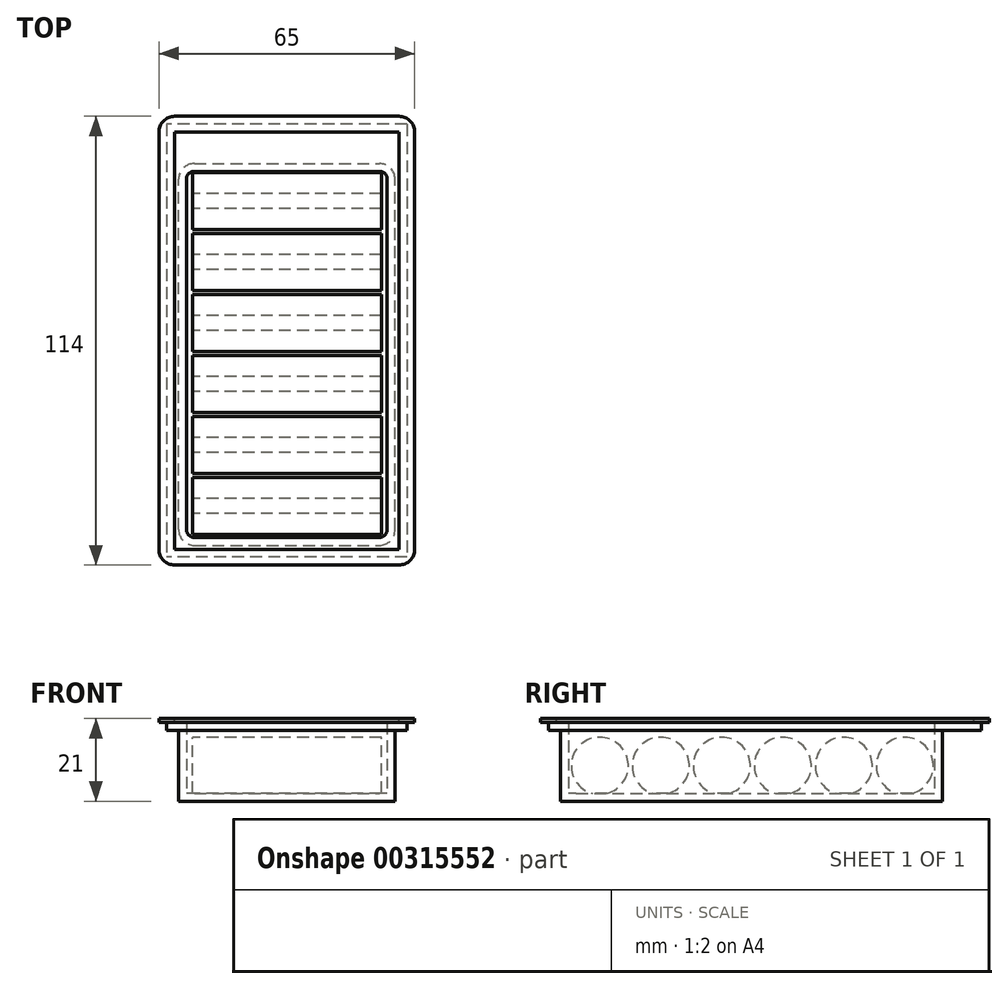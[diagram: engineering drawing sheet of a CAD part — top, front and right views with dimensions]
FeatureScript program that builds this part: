
annotation { "Feature Type Name" : "Feature", "Feature Type Description" : "" }
export const myFeature = defineFeature(function(context is Context, id is Id, definition is map)
    precondition{}
    {
        {
            var Q0;
            Q0=qCreatedBy(makeId("Top.planeOp"),FACE);
            var sketch = newSketch(context, id + "F0", { "sketchPlane" : qUnion([Q0])});
            skLineSegment(sketch, "E0.bottom", {"start": v(28.5, 57) * mm, "end": v(-28.5, 57) * mm});
            skLineSegment(sketch, "E0.top", {"start": v(28.5, -57) * mm, "end": v(-28.5, -57) * mm});
            skLineSegment(sketch, "E0.left", {"start": v(32.5, 53) * mm, "end": v(32.5, -53) * mm});
            skLineSegment(sketch, "E0.right", {"start": v(-32.5, 53) * mm, "end": v(-32.5, -53) * mm});
            skPoint(sketch, "E0.middle", {"position": v(0, 0) * mm});
            skPoint(sketch, "E1.visualSharp", {"position": v(-32.5, 57) * mm});
            skArc(sketch, "E1.filletArc", {"start": v(-28.5, 57) * mm, "mid": v(-31.33, 55.83) * mm, "end": v(-32.5, 53) * mm});
            skPoint(sketch, "E2.visualSharp", {"position": v(32.5, 57) * mm});
            skArc(sketch, "E2.filletArc", {"start": v(32.5, 53) * mm, "mid": v(31.33, 55.83) * mm, "end": v(28.5, 57) * mm});
            skPoint(sketch, "E3.visualSharp", {"position": v(32.5, -57) * mm});
            skArc(sketch, "E3.filletArc", {"start": v(28.5, -57) * mm, "mid": v(31.33, -55.83) * mm, "end": v(32.5, -53) * mm});
            skPoint(sketch, "E4.visualSharp", {"position": v(-32.5, -57) * mm});
            skArc(sketch, "E4.filletArc", {"start": v(-32.5, -53) * mm, "mid": v(-31.33, -55.83) * mm, "end": v(-28.5, -57) * mm});
            skSolve(sketch);
        }
        {
            var Q0;
            Q0 = qSketchRegion(id + "F0", true);
            extrude(context, id + "F1", {"entities" : qUnion([Q0]), "depth" : 1 * mm});
        }
        {
            var Q0;
            Q0=qCreatedBy(makeId("Top.planeOp"),FACE);
            var sketch = newSketch(context, id + "F2", { "sketchPlane" : qUnion([Q0])});
            skLineSegment(sketch, "E5.bottom", {"start": v(30.5, 55) * mm, "end": v(-30.5, 55) * mm});
            skLineSegment(sketch, "E5.top", {"start": v(30.5, -55) * mm, "end": v(-30.5, -55) * mm});
            skLineSegment(sketch, "E5.left", {"start": v(30.5, 55) * mm, "end": v(30.5, -55) * mm});
            skLineSegment(sketch, "E5.right", {"start": v(-30.5, 55) * mm, "end": v(-30.5, -55) * mm});
            skPoint(sketch, "E5.middle", {"position": v(0, 0) * mm});
            skSolve(sketch);
        }
        {
            var Q0;
            Q0 = qSketchRegion(id + "F2", true);
            extrude(context, id + "F3", {"entities" : qUnion([Q0]), "operationType" : NewBodyOperationType.ADD, "oppositeDirection" : true, "depth" : 2 * mm});
        }
        {
            var Q0;
            Q0=makeQuery(id+"F3.opExtrude","CAP_FACE",FACE,{"disambiguationData":[OSD([sQuery(id+"F2.wireOp",EDGE,"E5.bottom"),sQuery(id+"F2.wireOp",EDGE,"E5.top"),sQuery(id+"F2.wireOp",EDGE,"E5.left"),sQuery(id+"F2.wireOp",EDGE,"E5.right")])],"isStart":false});
            var sketch = newSketch(context, id + "F4", { "sketchPlane" : qUnion([Q0])});
            skLineSegment(sketch, "E6.bottom", {"start": v(-23.5, 52) * mm, "end": v(23.5, 52) * mm});
            skLineSegment(sketch, "E6.top", {"start": v(-23.5, -45) * mm, "end": v(23.5, -45) * mm});
            skLineSegment(sketch, "E6.left", {"start": v(-27.5, 48) * mm, "end": v(-27.5, -41) * mm});
            skLineSegment(sketch, "E6.right", {"start": v(27.5, 48) * mm, "end": v(27.5, -41) * mm});
            skPoint(sketch, "E7.visualSharp", {"position": v(-27.5, 52) * mm});
            skArc(sketch, "E7.filletArc", {"start": v(-23.5, 52) * mm, "mid": v(-26.33, 50.83) * mm, "end": v(-27.5, 48) * mm});
            skPoint(sketch, "E8.visualSharp", {"position": v(27.5, 52) * mm});
            skArc(sketch, "E8.filletArc", {"start": v(27.5, 48) * mm, "mid": v(26.33, 50.83) * mm, "end": v(23.5, 52) * mm});
            skPoint(sketch, "E9.visualSharp", {"position": v(27.5, -45) * mm});
            skArc(sketch, "E9.filletArc", {"start": v(23.5, -45) * mm, "mid": v(26.33, -43.83) * mm, "end": v(27.5, -41) * mm});
            skPoint(sketch, "E10.visualSharp", {"position": v(-27.5, -45) * mm});
            skArc(sketch, "E10.filletArc", {"start": v(-27.5, -41) * mm, "mid": v(-26.33, -43.83) * mm, "end": v(-23.5, -45) * mm});
            skSolve(sketch);
        }
        {
            var Q0;
            Q0 = qSketchRegion(id + "F4", true);
            extrude(context, id + "F5", {"entities" : qUnion([Q0]), "operationType" : NewBodyOperationType.ADD, "depth" : 18 * mm});
        }
        {
            var Q0;
            Q0=makeQuery(id+"F1.opExtrude","CAP_FACE",FACE,{"disambiguationData":[OSD([sQuery(id+"F0.wireOp",EDGE,"E0.bottom"),sQuery(id+"F0.wireOp",EDGE,"E0.top"),sQuery(id+"F0.wireOp",EDGE,"E0.left"),sQuery(id+"F0.wireOp",EDGE,"E0.right")])],"isStart":false});
            shell(context, id + "F6", {"entities" : qUnion([Q0]), "thickness" : 2 * mm});
        }
        {
            var Q0;
            Q0=qCreatedBy(makeId("Right.planeOp"),FACE);
            var sketch = newSketch(context, id + "F7", { "sketchPlane" : qUnion([Q0])});
            skCircle(sketch, "E11", {"center": v(35.5, -11) * mm, "radius": 7.25 * mm});
            skCircle(sketch, "E12.1.0.0", {"center": v(20, -11) * mm, "radius": 7.25 * mm});
            skCircle(sketch, "E12.2.0.0", {"center": v(4.5, -11) * mm, "radius": 7.25 * mm});
            skCircle(sketch, "E12.3.0.0", {"center": v(-11, -11) * mm, "radius": 7.25 * mm});
            skCircle(sketch, "E12.4.0.0", {"center": v(-26.5, -11) * mm, "radius": 7.25 * mm});
            skCircle(sketch, "E12.5.0.0", {"center": v(-42, -11) * mm, "radius": 7.25 * mm});
            skLineSegment(sketch, "E12.direction1", {"start": v(35, -11) * mm, "end": v(19.5, -11) * mm, "construction": true});
            skSolve(sketch);
        }
        {
            var Q0;
            Q0 = qSketchRegion(id + "F7", true);
            extrude(context, id + "F8", {"entities" : qUnion([Q0]), "operationType" : NewBodyOperationType.ADD, "depth" : 48 * mm, "symmetric" : true});
        }
    });
